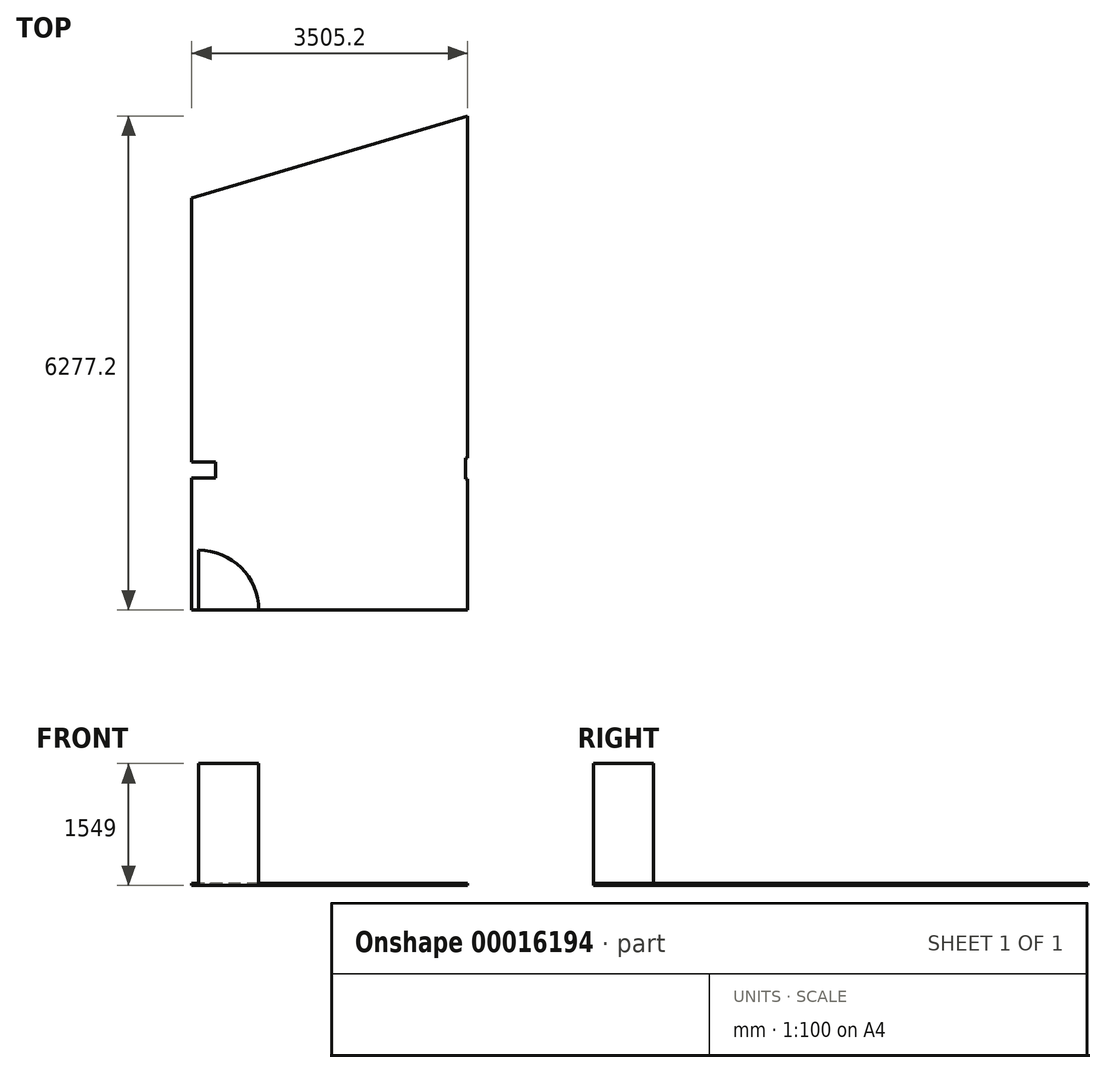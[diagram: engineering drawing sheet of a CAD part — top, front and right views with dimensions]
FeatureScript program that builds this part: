
annotation { "Feature Type Name" : "Feature", "Feature Type Description" : "" }
export const myFeature = defineFeature(function(context is Context, id is Id, definition is map)
    precondition{}
    {
        {
            var Q0;
            Q0=qCreatedBy(makeId("Top.planeOp"),FACE);
            var sketch = newSketch(context, id + "F0", { "sketchPlane" : qUnion([Q0])});
            skLineSegment(sketch, "E0", {"start": v(-2677.37, -3711.32) * mm, "end": v(827.83, -3711.32) * mm});
            skLineSegment(sketch, "E1", {"start": v(827.83, -3711.32) * mm, "end": v(827.83, -2044.22) * mm});
            skLineSegment(sketch, "E2", {"start": v(827.83, 2565.88) * mm, "end": v(-2677.37, 1521.08) * mm});
            skLineSegment(sketch, "E3", {"start": v(-2677.37, 1521.08) * mm, "end": v(-2677.37, -1831.72) * mm});
            skLineSegment(sketch, "E4.bottom", {"start": v(-2677.37, -1831.72) * mm, "end": v(-2372.57, -1831.72) * mm});
            skLineSegment(sketch, "E4.top", {"start": v(-2677.37, -2034.92) * mm, "end": v(-2372.57, -2034.92) * mm});
            skLineSegment(sketch, "E4.right", {"start": v(-2372.57, -1831.72) * mm, "end": v(-2372.57, -2034.92) * mm});
            skLineSegment(sketch, "E5.bottom", {"start": v(827.83, -2044.22) * mm, "end": v(802.43, -2044.22) * mm});
            skLineSegment(sketch, "E5.top", {"start": v(827.83, -1777.52) * mm, "end": v(802.43, -1777.52) * mm});
            skLineSegment(sketch, "E5.right", {"start": v(802.43, -2044.22) * mm, "end": v(802.43, -1777.52) * mm});
            skLineSegment(sketch, "E6.trimOffspring", {"start": v(-2677.37, -2034.92) * mm, "end": v(-2677.37, -3711.32) * mm});
            skLineSegment(sketch, "E7.trimOffspring", {"start": v(827.83, -1777.52) * mm, "end": v(827.83, 2565.88) * mm});
            skSolve(sketch);
        }
        {
            var Q0;
            Q0=makeQuery(id+"F0.imprint","IMPRINT",FACE,{"disambiguationData":[TD([[makeQuery(id+"F0.imprint","IMPRINT",EDGE,{"derivedFrom":sQuery(id+"F0.wireOp",EDGE,"E0")}),1.0]])]});
            extrude(context, id + "F1", {"entities" : qUnion([Q0]), "oppositeDirection" : true, "depth" : 25 * mm});
        }
        {
            var Q0;
            Q0=makeQuery(id+"F1.opExtrude","CAP_FACE",FACE,{"disambiguationData":[OSD([sQuery(id+"F0.wireOp",EDGE,"E0"),sQuery(id+"F0.wireOp",EDGE,"E1"),sQuery(id+"F0.wireOp",EDGE,"E2"),sQuery(id+"F0.wireOp",EDGE,"E3"),sQuery(id+"F0.wireOp",EDGE,"E4.bottom"),sQuery(id+"F0.wireOp",EDGE,"E4.top"),sQuery(id+"F0.wireOp",EDGE,"E4.right"),sQuery(id+"F0.wireOp",EDGE,"E5.bottom"),sQuery(id+"F0.wireOp",EDGE,"E5.top"),sQuery(id+"F0.wireOp",EDGE,"E5.right"),sQuery(id+"F0.wireOp",EDGE,"E6.trimOffspring"),sQuery(id+"F0.wireOp",EDGE,"E7.trimOffspring")])],"isStart":true});
            var sketch = newSketch(context, id + "F2", { "sketchPlane" : qUnion([Q0])});
            skLineSegment(sketch, "E8", {"start": v(-2588.47, -3711.32) * mm, "end": v(-1826.47, -3711.32) * mm});
            skLineSegment(sketch, "E9", {"start": v(-2588.47, -3711.32) * mm, "end": v(-2588.47, -2949.32) * mm});
            skArc(sketch, "E10", {"start": v(-1826.47, -3711.32) * mm, "mid": v(-2049.65, -3172.5) * mm, "end": v(-2588.47, -2949.32) * mm});
            skSolve(sketch);
        }
        {
            var Q0;
            Q0 = qSketchRegion(id + "F2", true);
            extrude(context, id + "F3", {"entities" : qUnion([Q0]), "operationType" : NewBodyOperationType.ADD, "depth" : 1524 * mm});
        }
    });
